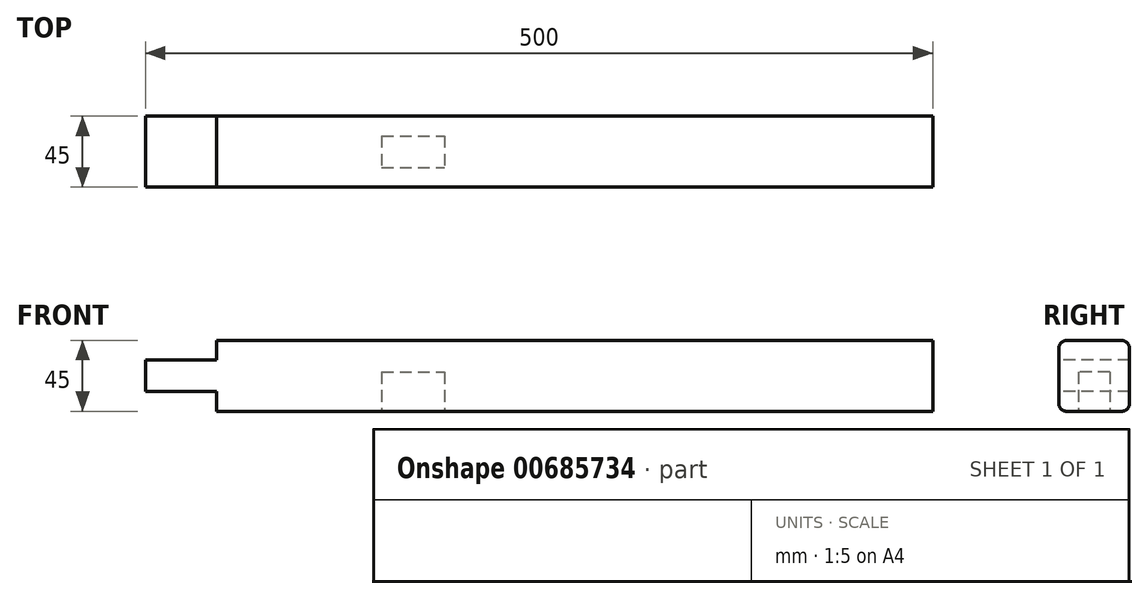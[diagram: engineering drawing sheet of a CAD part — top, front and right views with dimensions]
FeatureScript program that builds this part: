
annotation { "Feature Type Name" : "Feature", "Feature Type Description" : "" }
export const myFeature = defineFeature(function(context is Context, id is Id, definition is map)
    precondition{}
    {
        {
            var Q0;
            Q0=qCreatedBy(makeId("Right.planeOp"),FACE);
            var sketch = newSketch(context, id + "F0", { "sketchPlane" : qUnion([Q0])});
            skLineSegment(sketch, "E0.bottom", {"start": v(0, 0) * mm, "end": v(45, 0) * mm});
            skLineSegment(sketch, "E0.top", {"start": v(0, 45) * mm, "end": v(45, 45) * mm});
            skLineSegment(sketch, "E0.left", {"start": v(0, 0) * mm, "end": v(0, 45) * mm});
            skLineSegment(sketch, "E0.right", {"start": v(45, 0) * mm, "end": v(45, 45) * mm});
            skSolve(sketch);
        }
        {
            var Q0;
            Q0=qSketchRegion(id+"F0",true);
            extrude(context, id + "F1", {"entities" : qUnion([Q0]), "endBound" : BoundingType.SYMMETRIC, "depth" : 500 * mm, "offsetDistance" : 25 * mm});
        }
        {
            var Q0;
            Q0=makeQuery(id+"F1.opExtrude","SWEPT_EDGE",EDGE,{"disambiguationData":[OSD([sQuery(id+"F0.wireOp",EDGE,"E0.top"),sQuery(id+"F0.wireOp",EDGE,"E0.left")])]});
            var Q1;
            Q1=makeQuery(id+"F1.opExtrude","SWEPT_EDGE",EDGE,{"disambiguationData":[OSD([sQuery(id+"F0.wireOp",EDGE,"E0.top"),sQuery(id+"F0.wireOp",EDGE,"E0.right")])]});
            var Q2;
            Q2=makeQuery(id+"F1.opExtrude","SWEPT_EDGE",EDGE,{"disambiguationData":[OSD([sQuery(id+"F0.wireOp",EDGE,"E0.bottom"),sQuery(id+"F0.wireOp",EDGE,"E0.left")])]});
            var Q3;
            Q3=makeQuery(id+"F1.opExtrude","SWEPT_EDGE",EDGE,{"disambiguationData":[OSD([sQuery(id+"F0.wireOp",EDGE,"E0.bottom"),sQuery(id+"F0.wireOp",EDGE,"E0.right")])]});
            fillet(context, id + "F2", {"entities" : qUnion([Q0, Q1, Q2, Q3]), "radius" : 5 * mm, "tangentPropagation" : true, "allowEdgeOverflow" : false});
        }
        {
            var Q0;
            Q0=makeQuery(id+"F1.opExtrude","SWEPT_FACE",FACE,{"disambiguationData":[OSD([sQuery(id+"F0.wireOp",EDGE,"E0.left")])]});
            var sketch = newSketch(context, id + "F3", { "sketchPlane" : qUnion([Q0])});
            skLineSegment(sketch, "E1", {"start": v(-250, 22.5) * mm, "end": v(-205, 22.5) * mm, "construction": true});
            skLineSegment(sketch, "E2.bottom", {"start": v(-205, 12.5) * mm, "end": v(-250, 12.5) * mm});
            skLineSegment(sketch, "E2.top", {"start": v(-205, 32.5) * mm, "end": v(-250, 32.5) * mm});
            skLineSegment(sketch, "E2.left", {"start": v(-205, 12.5) * mm, "end": v(-205, 32.5) * mm, "construction": true});
            skLineSegment(sketch, "E2.right", {"start": v(-250, 12.5) * mm, "end": v(-250, 32.5) * mm});
            skPoint(sketch, "E2.middle", {"position": v(-227.5, 22.5) * mm});
            skLineSegment(sketch, "E3.bottom", {"start": v(-250, 32.5) * mm, "end": v(-205, 32.5) * mm});
            skLineSegment(sketch, "E3.top", {"start": v(-250, 45) * mm, "end": v(-205, 45) * mm});
            skLineSegment(sketch, "E3.left", {"start": v(-250, 32.5) * mm, "end": v(-250, 45) * mm});
            skLineSegment(sketch, "E3.right", {"start": v(-205, 32.5) * mm, "end": v(-205, 45) * mm});
            skLineSegment(sketch, "E4.bottom", {"start": v(-250, 12.5) * mm, "end": v(-205, 12.5) * mm});
            skLineSegment(sketch, "E4.top", {"start": v(-250, 0) * mm, "end": v(-205, 0) * mm});
            skLineSegment(sketch, "E4.left", {"start": v(-250, 12.5) * mm, "end": v(-250, 0) * mm});
            skLineSegment(sketch, "E4.right", {"start": v(-205, 12.5) * mm, "end": v(-205, 0) * mm});
            skSolve(sketch);
        }
        {
            var Q0;
            Q0=qSketchRegion(id+"F3",true);
            extrude(context, id + "F4", {"entities" : qUnion([Q0]), "operationType" : NewBodyOperationType.REMOVE, "endBound" : BoundingType.THROUGH_ALL, "oppositeDirection" : true, "depth" : 25 * mm, "offsetDistance" : 25 * mm});
        }
        {
            var Q0;
            Q0=makeQuery(id+"F1.opExtrude","CAP_FACE",FACE,{"disambiguationData":[OSD([sQuery(id+"F0.wireOp",EDGE,"E0.bottom"),sQuery(id+"F0.wireOp",EDGE,"E0.top"),sQuery(id+"F0.wireOp",EDGE,"E0.left"),sQuery(id+"F0.wireOp",EDGE,"E0.right")])],"isStart":true});
            var sketch = newSketch(context, id + "F5", { "sketchPlane" : qUnion([Q0])});
            skLineSegment(sketch, "E5.bottom", {"start": v(130, 32.5) * mm, "end": v(170, 32.5) * mm});
            skLineSegment(sketch, "E5.top", {"start": v(130, 12.5) * mm, "end": v(170, 12.5) * mm});
            skLineSegment(sketch, "E5.left", {"start": v(130, 32.5) * mm, "end": v(130, 12.5) * mm});
            skLineSegment(sketch, "E5.right", {"start": v(170, 32.5) * mm, "end": v(170, 12.5) * mm});
            skPoint(sketch, "E5.middle", {"position": v(150, 22.5) * mm});
            skPoint(sketch, "E5.middle.positionSnap0", {"position": v(0, 22.5) * mm});
            skPoint(sketch, "E5.centerSnap0", {"position": v(0, 22.5) * mm});
            skSolve(sketch);
        }
        {
            var Q0;
            Q0=qSketchRegion(id+"F5",true);
            extrude(context, id + "F6", {"entities" : qUnion([Q0]), "operationType" : NewBodyOperationType.REMOVE, "oppositeDirection" : true, "depth" : 25 * mm, "offsetDistance" : 25 * mm});
        }
        {
            var Q0;
            Q0=makeQuery(id+"F1.opExtrude","SWEPT_FACE",FACE,{"disambiguationData":[OSD([sQuery(id+"F0.wireOp",EDGE,"E0.bottom")])]});
            var sketch = newSketch(context, id + "F7", { "sketchPlane" : qUnion([Q0])});
            skLineSegment(sketch, "E6.bottom", {"start": v(-100, -32.5) * mm, "end": v(-60, -32.5) * mm});
            skLineSegment(sketch, "E6.top", {"start": v(-100, -12.5) * mm, "end": v(-60, -12.5) * mm});
            skLineSegment(sketch, "E6.left", {"start": v(-100, -32.5) * mm, "end": v(-100, -12.5) * mm});
            skLineSegment(sketch, "E6.right", {"start": v(-60, -32.5) * mm, "end": v(-60, -12.5) * mm});
            skPoint(sketch, "E6.middle", {"position": v(-80, -22.5) * mm});
            skPoint(sketch, "E6.middle.positionSnap0", {"position": v(-205, -22.5) * mm});
            skPoint(sketch, "E6.centerSnap0", {"position": v(-205, -22.5) * mm});
            skSolve(sketch);
        }
        {
            var Q0;
            Q0=qSketchRegion(id+"F7",true);
            extrude(context, id + "F8", {"entities" : qUnion([Q0]), "operationType" : NewBodyOperationType.REMOVE, "oppositeDirection" : true, "depth" : 25 * mm, "offsetDistance" : 25 * mm});
        }
    });
